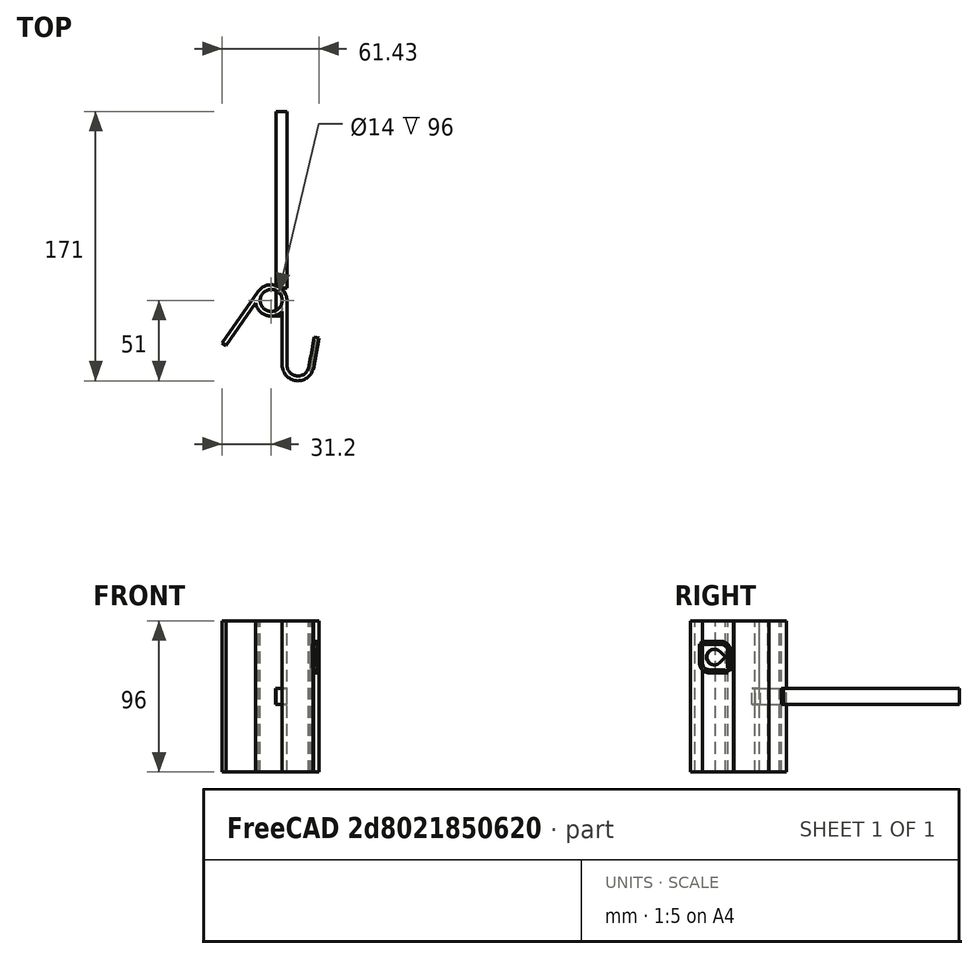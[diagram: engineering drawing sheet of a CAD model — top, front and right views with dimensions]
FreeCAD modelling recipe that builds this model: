
FCSTD DOCUMENT  (FreeCAD 0.15R4671 (Git))
Label: business-card-holder
License: All rights reserved
LicenseURL: http://en.wikipedia.org/wiki/All_rights_reserved
objects: Part::Box×13, Part::Cut×10, Part::Fuse×6, Part::Cylinder×5, Part::Fillet×4
note: 38 computed .brp shape members not serialized (recipe doc carries the construction recipe); baked Part::Feature solids carry a one-line shape summary decoded from their .brp

FEATURE [Part::Cylinder] Cylinder
  Angle = 360
  Height = 96
  Placement = pos=(-6,42,0) rot=(0,0,1;0rad)
  Radius = 10
FEATURE [Part::Cylinder] Cylinder002
  Angle = 360
  Height = 96
  Placement = pos=(11,1,0) rot=(0,0,1;0rad)
  Radius = 10
FEATURE [Part::Box] Box001  label="Cube001"
  Height = 96
  Length = 3
  Placement = pos=(-37.2,15,0) rot=(0,0,-1;0.610865rad)
  Width = 40
FEATURE [Part::Box] Box002  label="Cube002"
  Height = 96
  Length = 3
  Placement = pos=(1,1,0) rot=(0,0,1;0rad)
  Width = 40
FEATURE [Part::Box] Box003  label="Cube003"
  Height = 96
  Length = 3
  Placement = pos=(17.8,-0.9,0) rot=(0,0,-1;0.174533rad)
  Width = 20
FEATURE [Part::Cylinder] Cylinder003
  Angle = 360
  Height = 100
  Placement = pos=(-6,42,-2) rot=(0,0,1;0rad)
  Radius = 7
FEATURE [Part::Cylinder] Cylinder004
  Angle = 360
  Height = 102
  Placement = pos=(11,1,-2) rot=(0,0,1;0rad)
  Radius = 7
FEATURE [Part::Box] Box  label="Cube004"
  Height = 96
  Length = 3
  Placement = pos=(4,1,0) rot=(0,0,1;0rad)
  Width = 40
FEATURE [Part::Box] Box004  label="Cube005"
  Height = 96
  Length = 3
  Placement = pos=(14.8,-0.5,0) rot=(0,0,-1;0.174533rad)
  Width = 20
FEATURE [Part::Box] Box005  label="Cube"
  Height = 100
  Length = 12
  Placement = pos=(5,6,-1) rot=(0,0,-1;0.15708rad)
  Width = 10
FEATURE [Part::Cylinder] Cylinder005
  Angle = 360
  Height = 3
  Radius = 5
FEATURE [Part::Box] Box006  label="Cube006"
  Height = 3
  Length = 5
  Placement = pos=(0,-7.071,0) rot=(0,0,1;0.785398rad)
  Width = 5
FEATURE [Part::Box] Box007  label="Cube007"
  Height = 6
  Length = 16
  Placement = pos=(-8,-8.5,-1) rot=(0,0,1;0rad)
  Width = 16
FEATURE [Part::Box] Box008  label="Cube008"
  Height = 10
  Length = 34
  Placement = pos=(-10.4,-12,-3) rot=(0,0,1;0.785398rad)
  Width = 2
FEATURE [Part::Box] Box009  label="Cube009"
  Height = 3
  Length = 20
  Placement = pos=(-10,-10.5,0) rot=(0,0,1;0rad)
  Width = 20
FEATURE [Part::Fillet] Fillet
  Base = -> Box007
  Edges = 1 edges r=4: [Edge3]
FEATURE [Part::Fillet] Fillet001
  Base = -> Fillet
  Edges = 1 edges r=4: [Edge12]
FEATURE [Part::Fillet] Fillet002
  Base = -> Box009
  Edges = 1 edges r=6: [Edge5]
FEATURE [Part::Fillet] Fillet003
  Base = -> Fillet002
  Edges = 1 edges r=6: [Edge12]
FEATURE [Part::Cut] Cut005
  Base = -> Fillet003
  Tool = -> Fillet001
FEATURE [Part::Cut] Cut006
  Base = -> Cut005
  Tool = -> Box008
FEATURE [Part::Fuse] Fusion004
  Base = -> Cylinder005
  Tool = -> Box006
FEATURE [Part::Fuse] Fusion005  label="rrp-logo"
  Base = -> Cut006
  Placement = pos=(20.5,6.49441,73) rot=(0.705474,-0.06793,0.705473;3.00595rad)
  Tool = -> Fusion004
FEATURE [Part::Box] Box010  label="Cube010"
  Height = 10
  Length = 7
  Placement = pos=(-3,32,43) rot=(0,0,1;0rad)
  Width = 130
FEATURE [Part::Box] Box011  label="Cube011"
  Height = 13
  Length = 10
  Placement = pos=(0.9,25,41) rot=(0,0,1;0rad)
  Width = 25
FEATURE [Part::Cut] Cut008  label="stick"
  Base = -> Box010
  Tool = -> Box011
FEATURE [Part::Box] Box012  label="Cube012"
  Height = 10.4
  Length = 4.4
  Placement = pos=(-3.2,30,42.8) rot=(0,0,1;0rad)
  Width = 25
FEATURE [Part::Fuse] Fusion
  Base = -> Cylinder
  Tool = -> Box001
FEATURE [Part::Fuse] Fusion006
  Base = -> Box002
  Tool = -> Fusion
FEATURE [Part::Fuse] Fusion007
  Base = -> Cylinder002
  Tool = -> Fusion006
FEATURE [Part::Cut] Cut
  Base = -> Fusion007
  Tool = -> Cylinder004
FEATURE [Part::Cut] Cut009
  Base = -> Cut
  Tool = -> Cylinder003
FEATURE [Part::Cut] Cut010
  Base = -> Cut009
  Tool = -> Box012
FEATURE [Part::Cut] Cut011
  Base = -> Cut010
  Tool = -> Box
FEATURE [Part::Fuse] Fusion008
  Base = -> Box003
  Tool = -> Cut011
FEATURE [Part::Cut] Cut012
  Base = -> Fusion008
  Tool = -> Box004
FEATURE [Part::Cut] Cut013
  Base = -> Cut012
  Tool = -> Box005
FEATURE [Part::Cut] Cut014  label="holder"
  Base = -> Cut013
  Tool = -> Fusion005
